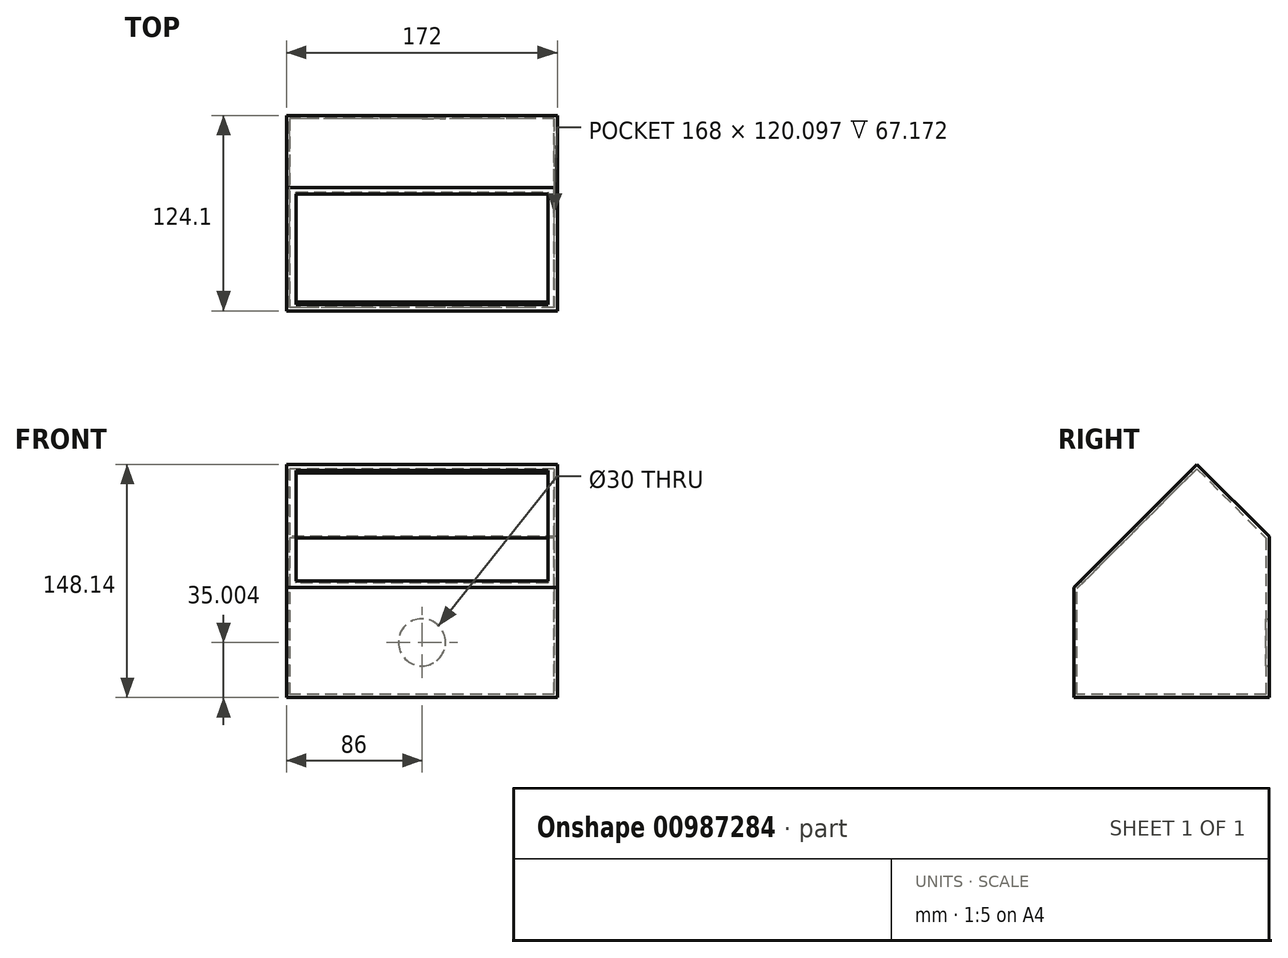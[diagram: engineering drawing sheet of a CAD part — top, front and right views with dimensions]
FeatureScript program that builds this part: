
annotation { "Feature Type Name" : "Feature", "Feature Type Description" : "" }
export const myFeature = defineFeature(function(context is Context, id is Id, definition is map)
    precondition{}
    {
        {
            var Q0;
            Q0=qCreatedBy(makeId("Right.planeOp"),FACE);
            var sketch = newSketch(context, id + "F0", { "sketchPlane" : qUnion([Q0])});
            skLineSegment(sketch, "E0", {"start": v(17.16, 48.46) * mm, "end": v(-60.98, -29.68) * mm});
            skLineSegment(sketch, "E1", {"start": v(63.12, 2.5) * mm, "end": v(17.16, 48.46) * mm});
            skLineSegment(sketch, "E2", {"start": v(-60.98, -29.68) * mm, "end": v(-60.98, -99.68) * mm});
            skLineSegment(sketch, "E3", {"start": v(-60.98, -99.68) * mm, "end": v(63.12, -99.68) * mm});
            skLineSegment(sketch, "E4", {"start": v(63.12, -99.68) * mm, "end": v(63.12, 2.5) * mm});
            skLineSegment(sketch, "E5.0", {"start": v(-58.98, -97.68) * mm, "end": v(61.12, -97.68) * mm});
            skLineSegment(sketch, "E5.1", {"start": v(-58.98, -30.5) * mm, "end": v(-58.98, -97.68) * mm});
            skLineSegment(sketch, "E5.2", {"start": v(61.12, -97.68) * mm, "end": v(61.12, 1.67) * mm});
            skLineSegment(sketch, "E5.3", {"start": v(61.12, 1.67) * mm, "end": v(17.16, 45.63) * mm});
            skLineSegment(sketch, "E5.4", {"start": v(17.16, 45.63) * mm, "end": v(-58.98, -30.5) * mm});
            skSolve(sketch);
        }
        {
            var Q0;
            Q0=makeQuery(id+"F0.imprint","IMPRINT",FACE,{"disambiguationData":[TD([[makeQuery(id+"F0.imprint","IMPRINT",EDGE,{"derivedFrom":sQuery(id+"F0.wireOp",EDGE,"E0")}),1.0]])]});
            extrude(context, id + "F1", {"entities" : qUnion([Q0]), "endBound" : BoundingType.SYMMETRIC, "depth" : 172 * mm, "offsetDistance" : 25 * mm});
        }
        {
            var Q0;
            Q0=makeQuery(id+"F1.opExtrude","SWEPT_FACE",FACE,{"disambiguationData":[OSD([sQuery(id+"F0.wireOp",EDGE,"E0")])]});
            var sketch = newSketch(context, id + "F2", { "sketchPlane" : qUnion([Q0])});
            skLineSegment(sketch, "E6.0", {"start": v(-80, 40.65) * mm, "end": v(-80, -58.35) * mm});
            skLineSegment(sketch, "E6.1", {"start": v(80, 40.65) * mm, "end": v(-80, 40.65) * mm});
            skLineSegment(sketch, "E6.2", {"start": v(80, -58.35) * mm, "end": v(80, 40.65) * mm});
            skLineSegment(sketch, "E6.3", {"start": v(-80, -58.35) * mm, "end": v(80, -58.35) * mm});
            skSolve(sketch);
        }
        {
            var Q0;
            Q0=makeQuery(id+"F2.imprint","IMPRINT",FACE,{"disambiguationData":[TD([[makeQuery(id+"F2.imprint","IMPRINT",EDGE,{"derivedFrom":sQuery(id+"F2.wireOp",EDGE,"E6.0")}),1.0]])]});
            extrude(context, id + "F3", {"entities" : qUnion([Q0]), "operationType" : NewBodyOperationType.REMOVE, "oppositeDirection" : true, "depth" : 25 * mm, "offsetDistance" : 25 * mm});
        }
        {
            var Q0;
            Q0=makeQuery(id+"F1.opExtrude","SWEPT_FACE",FACE,{"disambiguationData":[OSD([sQuery(id+"F0.wireOp",EDGE,"E4")])]});
            var sketch = newSketch(context, id + "F4", { "sketchPlane" : qUnion([Q0])});
            skCircle(sketch, "E7", {"center": v(0, -64.68) * mm, "radius": 15 * mm});
            skSolve(sketch);
        }
        {
            var Q0;
            Q0=qSketchRegion(id+"F4",true);
            extrude(context, id + "F5", {"entities" : qUnion([Q0]), "operationType" : NewBodyOperationType.REMOVE, "oppositeDirection" : true, "depth" : 25 * mm, "offsetDistance" : 25 * mm});
        }
        {
            var Q0;
            Q0=makeQuery(id+"F1.opExtrude","CAP_FACE",FACE,{"disambiguationData":[OSD([sQuery(id+"F0.wireOp",EDGE,"E0"),sQuery(id+"F0.wireOp",EDGE,"E1"),sQuery(id+"F0.wireOp",EDGE,"E2"),sQuery(id+"F0.wireOp",EDGE,"E3"),sQuery(id+"F0.wireOp",EDGE,"E4"),sQuery(id+"F0.wireOp",EDGE,"E5.0"),sQuery(id+"F0.wireOp",EDGE,"E5.1"),sQuery(id+"F0.wireOp",EDGE,"E5.2"),sQuery(id+"F0.wireOp",EDGE,"E5.3"),sQuery(id+"F0.wireOp",EDGE,"E5.4")])],"isStart":false});
            var sketch = newSketch(context, id + "F6", { "sketchPlane" : qUnion([Q0])});
            skLineSegment(sketch, "E8", {"start": v(17.16, 48.46) * mm, "end": v(-60.98, -29.68) * mm});
            skLineSegment(sketch, "E9", {"start": v(-60.98, -29.68) * mm, "end": v(-60.98, -99.68) * mm});
            skLineSegment(sketch, "E10", {"start": v(-60.98, -99.68) * mm, "end": v(63.12, -99.68) * mm});
            skLineSegment(sketch, "E11", {"start": v(63.12, -99.68) * mm, "end": v(63.12, 2.5) * mm});
            skLineSegment(sketch, "E12", {"start": v(63.12, 2.5) * mm, "end": v(17.16, 48.46) * mm});
            skSolve(sketch);
        }
        {
            var Q0;
            Q0=qSketchRegion(id+"F6",true);
            extrude(context, id + "F7", {"entities" : qUnion([Q0]), "operationType" : NewBodyOperationType.ADD, "oppositeDirection" : true, "depth" : 2 * mm, "offsetDistance" : 25 * mm});
        }
        {
            var Q0;
            Q0=makeQuery(id+"F1.opExtrude","CAP_FACE",FACE,{"disambiguationData":[OSD([sQuery(id+"F0.wireOp",EDGE,"E0"),sQuery(id+"F0.wireOp",EDGE,"E1"),sQuery(id+"F0.wireOp",EDGE,"E2"),sQuery(id+"F0.wireOp",EDGE,"E3"),sQuery(id+"F0.wireOp",EDGE,"E4"),sQuery(id+"F0.wireOp",EDGE,"E5.0"),sQuery(id+"F0.wireOp",EDGE,"E5.1"),sQuery(id+"F0.wireOp",EDGE,"E5.2"),sQuery(id+"F0.wireOp",EDGE,"E5.3"),sQuery(id+"F0.wireOp",EDGE,"E5.4")])],"isStart":true});
            var sketch = newSketch(context, id + "F8", { "sketchPlane" : qUnion([Q0])});
            skLineSegment(sketch, "E13", {"start": v(-63.12, 2.5) * mm, "end": v(-17.16, 48.46) * mm});
            skLineSegment(sketch, "E14", {"start": v(-17.16, 48.46) * mm, "end": v(60.98, -29.68) * mm});
            skLineSegment(sketch, "E15", {"start": v(60.98, -29.68) * mm, "end": v(60.98, -99.68) * mm});
            skLineSegment(sketch, "E16", {"start": v(60.98, -99.68) * mm, "end": v(-63.12, -99.68) * mm});
            skLineSegment(sketch, "E17", {"start": v(-63.12, -99.68) * mm, "end": v(-63.12, 2.5) * mm});
            skSolve(sketch);
        }
        {
            var Q0;
            Q0=qSketchRegion(id+"F8",true);
            extrude(context, id + "F9", {"entities" : qUnion([Q0]), "operationType" : NewBodyOperationType.ADD, "oppositeDirection" : true, "depth" : 2 * mm, "offsetDistance" : 25 * mm});
        }
    });
